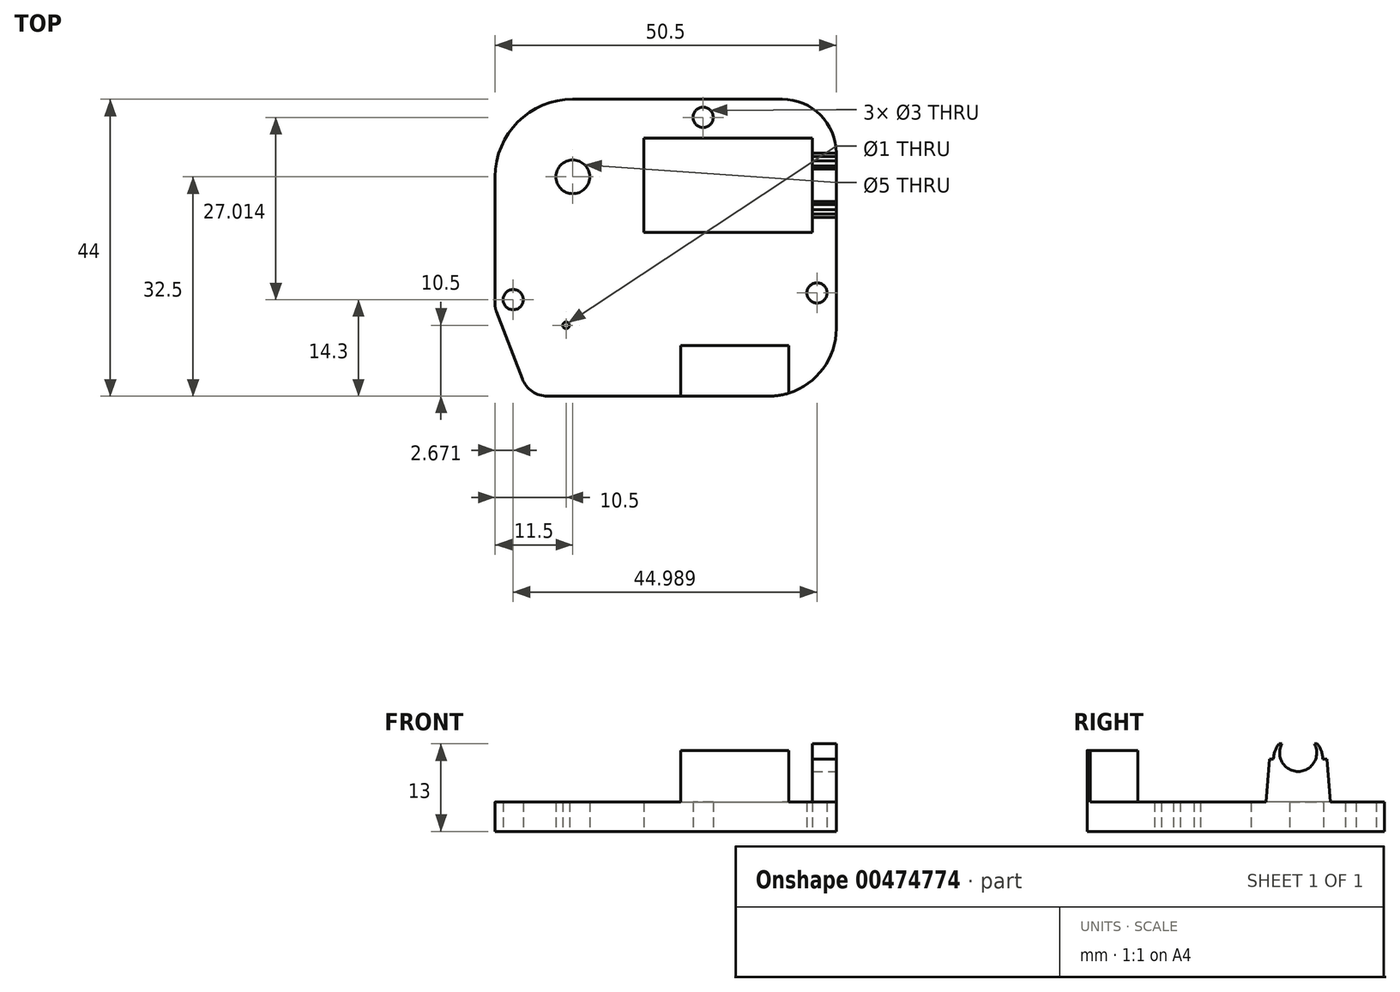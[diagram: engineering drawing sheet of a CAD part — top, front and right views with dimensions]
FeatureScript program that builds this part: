
annotation { "Feature Type Name" : "Feature", "Feature Type Description" : "" }
export const myFeature = defineFeature(function(context is Context, id is Id, definition is map)
    precondition{}
    {
        {
            var Q0;
            Q0=qCreatedBy(makeId("Top.planeOp"),FACE);
            var sketch = newSketch(context, id + "F0", { "sketchPlane" : qUnion([Q0])});
            skLineSegment(sketch, "E0.bottom", {"start": v(0, 0) * mm, "end": v(5, 0) * mm, "construction": true});
            skLineSegment(sketch, "E0.top", {"start": v(0, 44) * mm, "end": v(50.5, 44) * mm, "construction": true});
            skLineSegment(sketch, "E0.left", {"start": v(0, 0) * mm, "end": v(0, 13) * mm, "construction": true});
            skLineSegment(sketch, "E0.right", {"start": v(50.5, 0) * mm, "end": v(50.5, 44) * mm, "construction": true});
            skLineSegment(sketch, "E1", {"start": v(11.5, 44) * mm, "end": v(42.5, 44) * mm});
            skArc(sketch, "E2", {"start": v(50.5, 36) * mm, "mid": v(48.16, 41.66) * mm, "end": v(42.5, 44) * mm});
            skLineSegment(sketch, "E3", {"start": v(50.5, 36) * mm, "end": v(50.5, 10) * mm});
            skArc(sketch, "E4", {"start": v(11.5, 44) * mm, "mid": v(3.37, 40.63) * mm, "end": v(0, 32.5) * mm});
            skArc(sketch, "E5", {"start": v(40.5, 0) * mm, "mid": v(47.57, 2.93) * mm, "end": v(50.5, 10) * mm});
            skLineSegment(sketch, "E6", {"start": v(40.5, 0) * mm, "end": v(7.75, 0) * mm});
            skLineSegment(sketch, "E7", {"start": v(0, 32.5) * mm, "end": v(0, 13.46) * mm});
            skLineSegment(sketch, "E8", {"start": v(0.17, 12.57) * mm, "end": v(4.01, 2.56) * mm});
            skLineSegment(sketch, "E9", {"start": v(0, 13) * mm, "end": v(50.5, 13) * mm, "construction": true});
            skArc(sketch, "E10", {"start": v(0, 13.46) * mm, "mid": v(0.04, 13) * mm, "end": v(0.17, 12.57) * mm});
            skArc(sketch, "E11", {"start": v(4.01, 2.56) * mm, "mid": v(5.48, 0.7) * mm, "end": v(7.75, 0) * mm});
            skLineSegment(sketch, "E12.trimOffspring", {"start": v(0, 13.46) * mm, "end": v(0, 44) * mm, "construction": true});
            skLineSegment(sketch, "E13.trimOffspring", {"start": v(7.75, 0) * mm, "end": v(50.5, 0) * mm, "construction": true});
            skLineSegment(sketch, "E14.bottom", {"start": v(22, 38.25) * mm, "end": v(47, 38.25) * mm});
            skLineSegment(sketch, "E14.top", {"start": v(22, 24.25) * mm, "end": v(47, 24.25) * mm});
            skLineSegment(sketch, "E14.left", {"start": v(22, 38.25) * mm, "end": v(22, 24.25) * mm});
            skLineSegment(sketch, "E14.right", {"start": v(47, 38.25) * mm, "end": v(47, 24.25) * mm});
            skLineSegment(sketch, "E15", {"start": v(22, 31.25) * mm, "end": v(50.5, 31.25) * mm, "construction": true});
            skCircle(sketch, "E16", {"center": v(10.5, 10.5) * mm, "radius": 0.5 * mm});
            skCircle(sketch, "E17", {"center": v(11.5, 32.5) * mm, "radius": 2.5 * mm});
            skCircle(sketch, "E18", {"center": v(2.67, 14.3) * mm, "radius": 1.5 * mm});
            skCircle(sketch, "E19", {"center": v(47.66, 15.3) * mm, "radius": 1.5 * mm});
            skCircle(sketch, "E20", {"center": v(30.8, 41.31) * mm, "radius": 1.5 * mm});
            skSolve(sketch);
        }
        {
            var Q0;
            Q0 = qSketchRegion(id + "F0", true);
            extrude(context, id + "F1", {"entities" : qUnion([Q0]), "depth" : 4.4 * mm});
        }
        {
            var Q0;
            Q0=makeQuery(id+"F1.opExtrude","CAP_FACE",FACE,{"disambiguationData":[OSD([sQuery(id+"F0.wireOp",EDGE,"E1"),sQuery(id+"F0.wireOp",EDGE,"E2"),sQuery(id+"F0.wireOp",EDGE,"E3"),sQuery(id+"F0.wireOp",EDGE,"E4"),sQuery(id+"F0.wireOp",EDGE,"E5"),sQuery(id+"F0.wireOp",EDGE,"E6"),sQuery(id+"F0.wireOp",EDGE,"E7"),sQuery(id+"F0.wireOp",EDGE,"E8"),sQuery(id+"F0.wireOp",EDGE,"E10"),sQuery(id+"F0.wireOp",EDGE,"E11"),sQuery(id+"F0.wireOp",EDGE,"URUyEK2U-Yy7R-w5lx-aGi4-ZFB9Pn7TAm8G"),sQuery(id+"F0.wireOp",EDGE,"EzZ4k0Nr-0TFC-zg2q-6aTR-mPMdrYf2f0UB"),sQuery(id+"F0.wireOp",EDGE,"R58MSP0A-yrsf-6VZn-dFl0-iIUBZR48KmvA")])],"isStart":false});
            var sketch = newSketch(context, id + "F2", { "sketchPlane" : qUnion([Q0])});
            skLineSegment(sketch, "E21.top", {"start": v(50.5, 26.5) * mm, "end": v(47, 26.5) * mm});
            skLineSegment(sketch, "E21.right", {"start": v(47, 36) * mm, "end": v(47, 26.5) * mm});
            skLineSegment(sketch, "E22", {"start": v(47, 36) * mm, "end": v(50.5, 36) * mm});
            skLineSegment(sketch, "E23", {"start": v(50.5, 36) * mm, "end": v(50.5, 26.5) * mm});
            skLineSegment(sketch, "E24", {"start": v(47, 31.25) * mm, "end": v(50.5, 31.25) * mm, "construction": true});
            skSolve(sketch);
        }
        {
            var Q0;
            Q0 = qSketchRegion(id + "F2", true);
            extrude(context, id + "F3", {"entities" : qUnion([Q0]), "operationType" : NewBodyOperationType.ADD, "depth" : (13 - 4.4) * mm});
        }
        {
            var Q0;
            Q0=makeQuery(id+"F3.boolean.opBoolean","MERGE",FACE,{"derivedFrom":[makeQuery(id+"F1.opExtrude","SWEPT_FACE",FACE,{"disambiguationData":[OSD([sQuery(id+"F0.wireOp",EDGE,"E3")])]}),makeQuery(id+"F3.opExtrude","SWEPT_FACE",FACE,{"disambiguationData":[OSD([sQuery(id+"F2.wireOp",EDGE,"E23")])]})]});
            var sketch = newSketch(context, id + "F4", { "sketchPlane" : qUnion([Q0])});
            skCircle(sketch, "E25", {"center": v(31.25, 11.65) * mm, "radius": 2.75 * mm, "construction": true});
            skLineSegment(sketch, "E26", {"start": v(31.25, 13) * mm, "end": v(31.25, 0) * mm, "construction": true});
            skArc(sketch, "E27", {"start": v(28.85, 13) * mm, "mid": v(31.25, 8.9) * mm, "end": v(33.65, 13) * mm});
            skLineSegment(sketch, "E28", {"start": v(26.5, 4.4) * mm, "end": v(27, 10.7) * mm});
            skLineSegment(sketch, "E29", {"start": v(27, 10.7) * mm, "end": v(27.6, 10.7) * mm});
            skArc(sketch, "E30", {"start": v(28.42, 13) * mm, "mid": v(27.8, 11.92) * mm, "end": v(27.6, 10.7) * mm});
            skArc(sketch, "E31", {"start": v(34.9, 10.7) * mm, "mid": v(34.7, 11.92) * mm, "end": v(34.08, 13) * mm});
            skLineSegment(sketch, "E32", {"start": v(34.9, 10.7) * mm, "end": v(35.5, 10.7) * mm});
            skLineSegment(sketch, "E33", {"start": v(35.5, 10.7) * mm, "end": v(36, 4.4) * mm});
            skLineSegment(sketch, "E34", {"start": v(27.6, 10.7) * mm, "end": v(27.6, 13) * mm, "construction": true});
            skLineSegment(sketch, "E35", {"start": v(28.42, 13) * mm, "end": v(26.5, 13) * mm});
            skLineSegment(sketch, "E36", {"start": v(26.5, 13) * mm, "end": v(26.5, 4.4) * mm});
            skLineSegment(sketch, "E37", {"start": v(34.08, 13) * mm, "end": v(36, 13) * mm});
            skLineSegment(sketch, "E38", {"start": v(36, 13) * mm, "end": v(36, 4.4) * mm});
            skLineSegment(sketch, "E39", {"start": v(28.85, 13) * mm, "end": v(33.65, 13) * mm});
            skSolve(sketch);
        }
        {
            var Q0;
            Q0 = qSketchRegion(id + "F4", true);
            extrude(context, id + "F5", {"entities" : qUnion([Q0]), "operationType" : NewBodyOperationType.REMOVE, "endBound" : BoundingType.UP_TO_NEXT, "oppositeDirection" : true, "depth" : 25 * mm});
        }
        {
            var Q0;
            Q0=makeQuery(id+"F1.opExtrude","CAP_FACE",FACE,{"disambiguationData":[OSD([sQuery(id+"F0.wireOp",EDGE,"E1"),sQuery(id+"F0.wireOp",EDGE,"E2"),sQuery(id+"F0.wireOp",EDGE,"E3"),sQuery(id+"F0.wireOp",EDGE,"E4"),sQuery(id+"F0.wireOp",EDGE,"E5"),sQuery(id+"F0.wireOp",EDGE,"E6"),sQuery(id+"F0.wireOp",EDGE,"E7"),sQuery(id+"F0.wireOp",EDGE,"E8"),sQuery(id+"F0.wireOp",EDGE,"E10"),sQuery(id+"F0.wireOp",EDGE,"E11"),sQuery(id+"F0.wireOp",EDGE,"URUyEK2U-Yy7R-w5lx-aGi4-ZFB9Pn7TAm8G"),sQuery(id+"F0.wireOp",EDGE,"EzZ4k0Nr-0TFC-zg2q-6aTR-mPMdrYf2f0UB"),sQuery(id+"F0.wireOp",EDGE,"R58MSP0A-yrsf-6VZn-dFl0-iIUBZR48KmvA")])],"isStart":false});
            var sketch = newSketch(context, id + "F6", { "sketchPlane" : qUnion([Q0])});
            skLineSegment(sketch, "E40", {"start": v(27.5, 0) * mm, "end": v(27.5, 7.5) * mm});
            skLineSegment(sketch, "E41", {"start": v(27.5, 7.5) * mm, "end": v(43.5, 7.5) * mm});
            skLineSegment(sketch, "E42", {"start": v(43.5, 7.5) * mm, "end": v(43.5, 0.46) * mm});
            skLineSegment(sketch, "E43", {"start": v(27.5, 0) * mm, "end": v(40.5, 0) * mm});
            skArc(sketch, "E44", {"start": v(40.5, 0) * mm, "mid": v(42.02, 0.12) * mm, "end": v(43.5, 0.46) * mm});
            skSolve(sketch);
        }
        {
            var Q0;
            Q0 = qSketchRegion(id + "F6", true);
            extrude(context, id + "F7", {"entities" : qUnion([Q0]), "operationType" : NewBodyOperationType.ADD, "depth" : (12 - 4.4) * mm});
        }
    });
